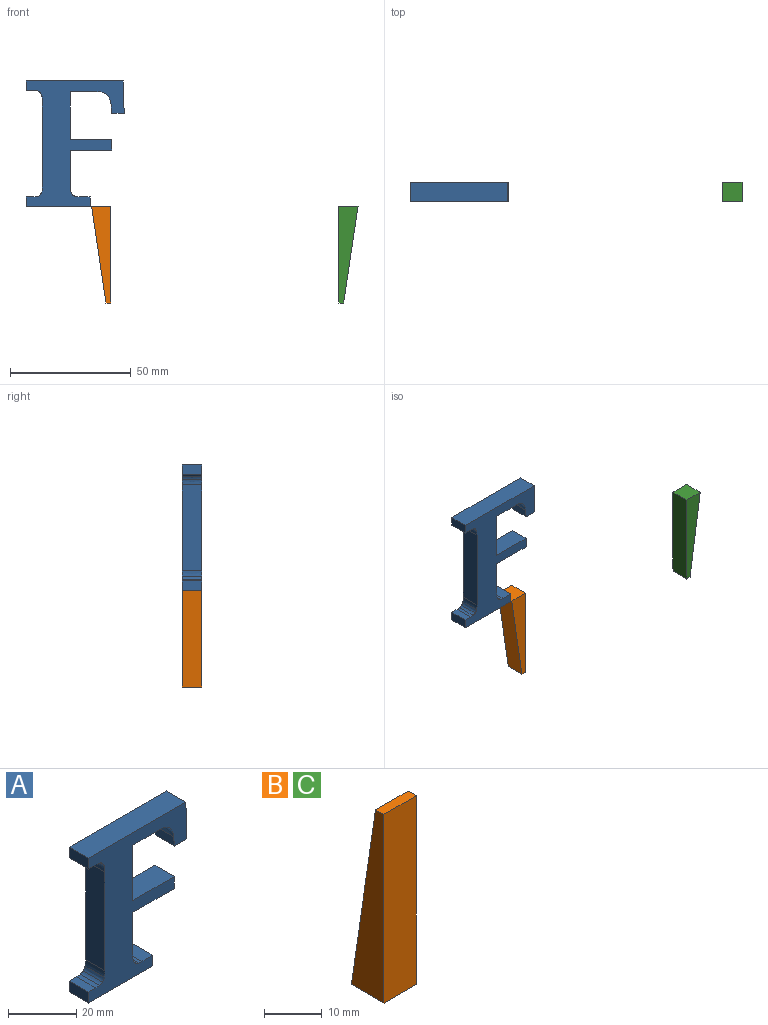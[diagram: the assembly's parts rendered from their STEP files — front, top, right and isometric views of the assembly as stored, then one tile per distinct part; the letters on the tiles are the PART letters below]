
ASSEMBLY  parts=3 mates=2
PART A: 34 faces, bbox 40.6x8x51.8 mm
  f0: plane 8x3.51mm, normal (-1,0,-0.1), area 28.2mm2, adj f1,f31,f32,f33
  f1: plane 8x5.07mm, normal (0,0,-1), area 40.6mm2, adj f0,f2,f32,f33
  f2: plane 13.37x8mm, normal (1,0,0.03), area 107mm2, adj f1,f3,f32,f33
  f3: plane 40.25x8mm, normal (0,0,1), area 322mm2, adj f2,f4,f32,f33
  f4: plane 8x3.84mm, normal (-1,0,0), area 30.7mm2, adj f3,f5,f32,f33
  f5: plane 8x3.05mm, normal (0,0,-1), area 24.4mm2, adj f4,f6,f32,f33
  f6: extruded ~8x1.45mm, area 11.7mm2, adj f5,f7,f32,f33
  f7: extruded ~8x1.19mm, area 10.8mm2, adj f6,f8,f32,f33
  f8: extruded ~8x1.33mm, area 12.5mm2, adj f7,f9,f32,f33
  f9: extruded ~8x2.32mm, area 18.8mm2, adj f8,f10,f32,f33
  f10: plane 35.4x8mm, normal (-1,0,0), area 283.2mm2, adj f9,f11,f32,f33
  f11: extruded ~8x2.29mm, area 18.5mm2, adj f10,f12,f32,f33
  f12: extruded ~8x1.31mm, area 12.4mm2, adj f11,f13,f32,f33
  f13: extruded ~8x1.19mm, area 10.7mm2, adj f12,f14,f32,f33
  f14: extruded ~8x1.45mm, area 11.7mm2, adj f13,f15,f32,f33
  f15: plane 8x3.05mm, normal (0,0,1), area 24.4mm2, adj f14,f16,f32,f33
  f16: plane 8x3.87mm, normal (-1,0,0), area 31mm2, adj f15,f17,f32,f33
  f17: plane 26.53x8mm, normal (0,0,-1), area 212.3mm2, adj f16,f18,f32,f33
  f18: plane 8x3.87mm, normal (1,0,0), area 31mm2, adj f17,f19,f32,f33
  f19: plane 8x4.51mm, normal (0,0,1), area 36mm2, adj f18,f20,f32,f33
  f20: extruded ~8x1.49mm, area 12mm2, adj f19,f21,f32,f33
  f21: extruded ~8x1.2mm, area 11.1mm2, adj f20,f22,f32,f33
  f22: extruded ~8x1.42mm, area 13.1mm2, adj f21,f23,f32,f33
  f23: extruded ~8x2.48mm, area 20.1mm2, adj f22,f24,f32,f33
  f24: plane 14.72x8mm, normal (1,0,0), area 117.7mm2, adj f23,f25,f32,f33
  f25: plane 17.24x8mm, normal (0,0,-1), area 137.9mm2, adj f24,f26,f32,f33
  f26: plane 8x4.29mm, normal (1,0,0), area 34.3mm2, adj f25,f27,f32,f33
  f27: plane 17.24x8mm, normal (0,0,1), area 137.9mm2, adj f26,f28,f32,f33
  f28: plane 19.83x8mm, normal (1,0,0), area 158.6mm2, adj f27,f29,f32,f33
  f29: plane 11.56x8mm, normal (0,0,-1), area 92.5mm2, adj f28,f30,f32,f33
  f30: extruded ~8x3.64mm, area 31.6mm2, adj f29,f31,f32,f33
  f31: extruded ~8x4.15mm, area 36.8mm2, adj f0,f30,f32,f33
  f32: plane 51.85x40.6mm, normal (0,-1,0), area 910.1mm2, adj f0,f1,f2,f3,f4,f5,f6,f7
  f33: plane 51.85x40.6mm, normal (0,1,0), area 910.1mm2, adj f0,f1,f2,f3,f4,f5,f6,f7
PART B: 6 faces, bbox 8x8x40 mm
  f0: plane 8x8mm, normal (0,0,-1), area 64mm2, adj f2,f3,f4,f5
  f1: plane 8x2mm, normal (0,0,1), area 16mm2, adj f2,f3,f4,f5
  f2: plane 40x8mm, normal (-1,0,0), area 200mm2, adj f0,f1,f3,f5
  f3: plane 40x8mm, normal (0,-1,0), area 320mm2, adj f0,f1,f2,f4
  f4: plane 40x8mm, normal (1,0,0), area 200mm2, adj f0,f1,f3,f5
  f5: plane 40x8mm, normal (0,0.99,0.15), area 323.5mm2, adj f0,f1,f2,f4
PART C: same geometry as B
PLACE A t=(21.02,44.27,-146.64)mm
PLACE B rot(axis=(0.71,-0.71,0),180deg) t=(96.3,44.27,-313.77)mm
PLACE C rot(axis=(0.71,0.71,0),180deg) t=(114.28,36.27,-313.77)mm
MATE planar C.f0 <-> A.f17  axis (0,0,1) through (156.4,40.27,-313.77)mm
MATE planar B.f0 <-> A.f17  axis (0,0,1) through (54.18,40.27,-313.77)mm
